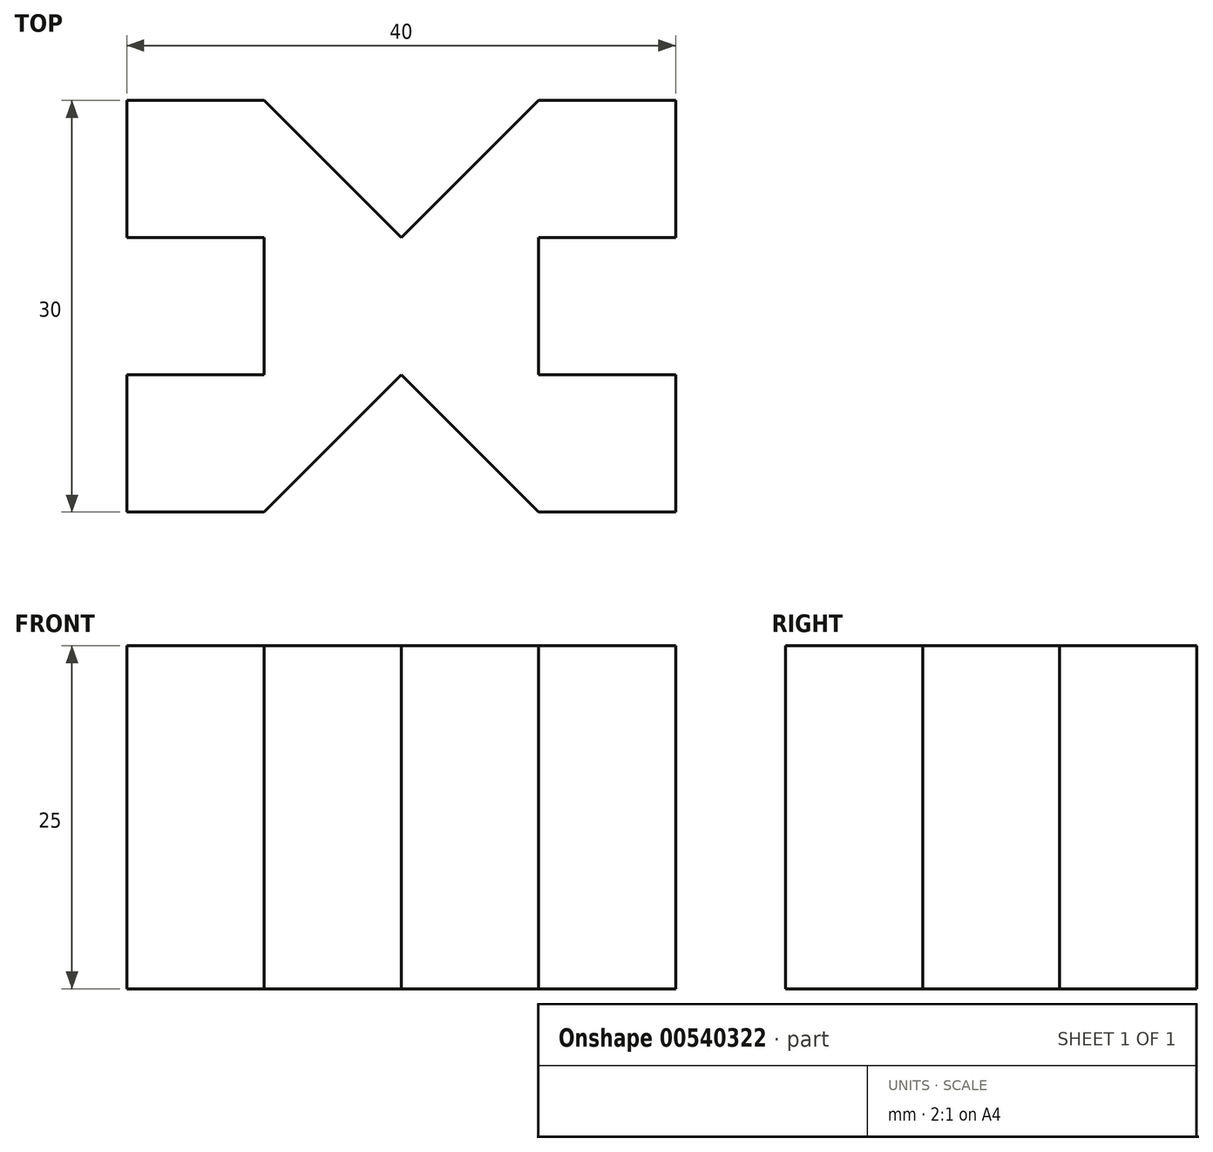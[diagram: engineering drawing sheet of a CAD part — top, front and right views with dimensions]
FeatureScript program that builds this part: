
annotation { "Feature Type Name" : "Feature", "Feature Type Description" : "" }
export const myFeature = defineFeature(function(context is Context, id is Id, definition is map)
    precondition{}
    {
        {
            var Q0;
            Q0=qCreatedBy(makeId("Top.planeOp"),FACE);
            var sketch = newSketch(context, id + "F0", { "sketchPlane" : qUnion([Q0])});
            skLineSegment(sketch, "E0", {"start": v(-20, 13.89) * mm, "end": v(-10, 13.89) * mm});
            skLineSegment(sketch, "E1", {"start": v(20, 13.89) * mm, "end": v(20, 3.89) * mm});
            skLineSegment(sketch, "E2", {"start": v(20, -16.11) * mm, "end": v(10, -16.11) * mm});
            skLineSegment(sketch, "E3", {"start": v(-20, -16.11) * mm, "end": v(-20, -6.11) * mm});
            skLineSegment(sketch, "E4", {"start": v(-20, 3.89) * mm, "end": v(-10, 3.89) * mm});
            skLineSegment(sketch, "E5", {"start": v(-10, 3.89) * mm, "end": v(-10, -6.11) * mm});
            skLineSegment(sketch, "E6", {"start": v(-10, -6.11) * mm, "end": v(-20, -6.11) * mm});
            skLineSegment(sketch, "E7.trimOffspring", {"start": v(-20, 3.89) * mm, "end": v(-20, 13.89) * mm});
            skLineSegment(sketch, "E8", {"start": v(20, 3.89) * mm, "end": v(10, 3.89) * mm});
            skLineSegment(sketch, "E9", {"start": v(10, 3.89) * mm, "end": v(10, -6.11) * mm});
            skLineSegment(sketch, "E10", {"start": v(10, -6.11) * mm, "end": v(20, -6.11) * mm});
            skLineSegment(sketch, "E11.trimOffspring", {"start": v(20, -6.11) * mm, "end": v(20, -16.11) * mm});
            skLineSegment(sketch, "E12", {"start": v(-10, -16.11) * mm, "end": v(0, -6.11) * mm});
            skLineSegment(sketch, "E13", {"start": v(0, -6.11) * mm, "end": v(10, -16.11) * mm});
            skLineSegment(sketch, "E14.trimOffspring", {"start": v(-10, -16.11) * mm, "end": v(-20, -16.11) * mm});
            skLineSegment(sketch, "E15", {"start": v(-10, 13.89) * mm, "end": v(0, 3.89) * mm});
            skLineSegment(sketch, "E16", {"start": v(0, 3.89) * mm, "end": v(10, 13.89) * mm});
            skLineSegment(sketch, "E17.trimOffspring", {"start": v(10, 13.89) * mm, "end": v(20, 13.89) * mm});
            skSolve(sketch);
        }
        {
            var Q0;
            Q0=makeQuery(id+"F0.imprint","IMPRINT",FACE,{"disambiguationData":[TD([[makeQuery(id+"F0.imprint","IMPRINT",EDGE,{"derivedFrom":sQuery(id+"F0.wireOp",EDGE,"E0")}),-1.0]])]});
            extrude(context, id + "F1", {"entities" : qUnion([Q0]), "depth" : 25 * mm, "offsetDistance" : 25 * mm});
        }
    });
